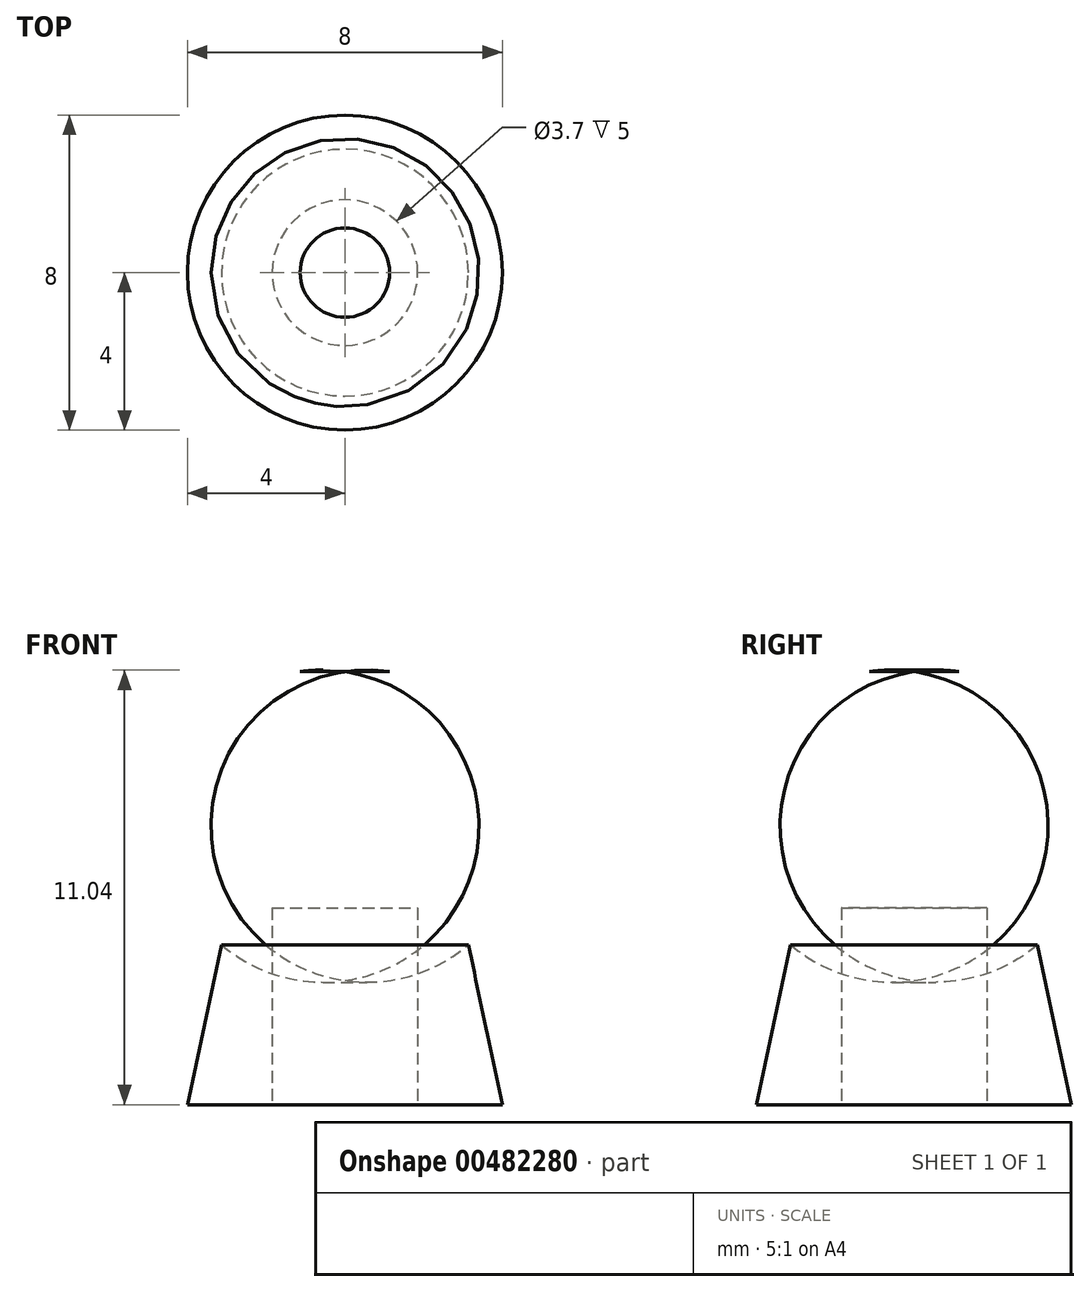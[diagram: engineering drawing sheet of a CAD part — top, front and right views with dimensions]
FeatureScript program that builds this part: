
annotation { "Feature Type Name" : "Feature", "Feature Type Description" : "" }
export const myFeature = defineFeature(function(context is Context, id is Id, definition is map)
    precondition{}
    {
        {
            var Q0;
            Q0=qCreatedBy(makeId("Front.planeOp"),FACE);
            var sketch = newSketch(context, id + "F0", { "sketchPlane" : qUnion([Q0])});
            skLineSegment(sketch, "E0", {"start": v(0, 0) * mm, "end": v(4, 0) * mm});
            skLineSegment(sketch, "E1", {"start": v(4, 0) * mm, "end": v(3.14, 4.06) * mm});
            skArc(sketch, "E2", {"start": v(3.14, 4.06) * mm, "mid": v(4.37, 8.18) * mm, "end": v(1.14, 11) * mm});
            skLineSegment(sketch, "E3", {"start": v(1.14, 11) * mm, "end": v(0, 11) * mm});
            skLineSegment(sketch, "E4", {"start": v(0, 19.3) * mm, "end": v(0, -15.74) * mm, "construction": true});
            skLineSegment(sketch, "E5", {"start": v(0, 11) * mm, "end": v(0, 0) * mm});
            skSolve(sketch);
        }
        {
            var Q0;
            Q0 = qSketchRegion(id + "F0", true);
            var Q1;
            Q1=sQuery(id+"F0.wireOp",EDGE,"E4");
            revolve(context, id + "F1", {"entities" : qUnion([Q0]), "axis" : qUnion([Q1]), "revolveType" : RevolveType.FULL});
        }
        {
            var Q0;
            Q0=makeQuery(id+"F1.opRevolve","SWEPT_FACE",FACE,{"disambiguationData":[OSD([sQuery(id+"F0.wireOp",EDGE,"E0")])]});
            var sketch = newSketch(context, id + "F2", { "sketchPlane" : qUnion([Q0])});
            skCircle(sketch, "E6", {"center": v(0, 0) * mm, "radius": 1.85 * mm});
            skSolve(sketch);
        }
        {
            var Q0;
            Q0 = qSketchRegion(id + "F2", true);
            extrude(context, id + "F3", {"entities" : qUnion([Q0]), "operationType" : NewBodyOperationType.REMOVE, "oppositeDirection" : true, "depth" : 5 * mm});
        }
    });
